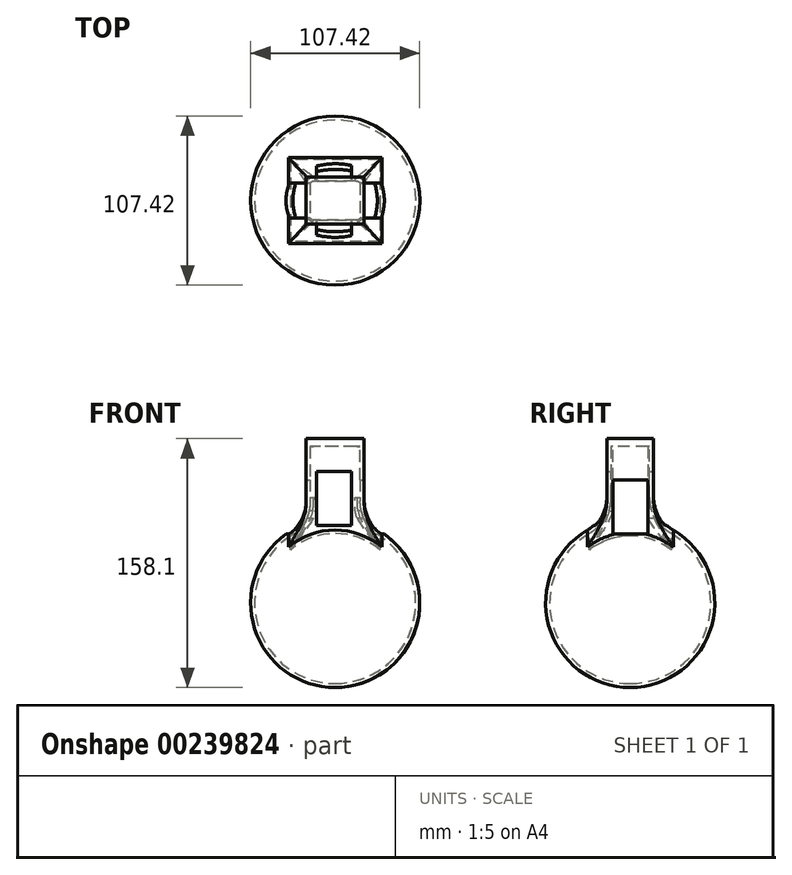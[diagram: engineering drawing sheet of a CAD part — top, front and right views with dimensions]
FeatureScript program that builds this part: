
annotation { "Feature Type Name" : "Feature", "Feature Type Description" : "" }
export const myFeature = defineFeature(function(context is Context, id is Id, definition is map)
    precondition{}
    {
        {
            var Q0;
            Q0=qCreatedBy(makeId("Front.planeOp"),FACE);
            var sketch = newSketch(context, id + "F0", { "sketchPlane" : qUnion([Q0])});
            skArc(sketch, "E0", {"start": v(0, 53.71) * mm, "mid": v(-53.71, 0) * mm, "end": v(0, -53.71) * mm});
            skLineSegment(sketch, "E1", {"start": v(0, 53.71) * mm, "end": v(0, -53.71) * mm});
            skSolve(sketch);
        }
        {
            var Q0;
            Q0 = qSketchRegion(id + "F0", true);
            var Q1;
            Q1=sQuery(id+"F0.wireOp",EDGE,"E1");
            revolve(context, id + "F1", {"entities" : qUnion([Q0]), "axis" : qUnion([Q1]), "revolveType" : RevolveType.FULL});
        }
        {
            var Q0;
            Q0=qCreatedBy(makeId("Top.planeOp"),FACE);
            var sketch = newSketch(context, id + "F2", { "sketchPlane" : qUnion([Q0])});
            skLineSegment(sketch, "E2.bottom", {"start": v(18.4, 14.82) * mm, "end": v(-18.4, 14.82) * mm});
            skLineSegment(sketch, "E2.top", {"start": v(18.4, -14.82) * mm, "end": v(-18.4, -14.82) * mm});
            skLineSegment(sketch, "E2.left", {"start": v(18.4, 14.82) * mm, "end": v(18.4, -14.82) * mm});
            skLineSegment(sketch, "E2.right", {"start": v(-18.4, 14.82) * mm, "end": v(-18.4, -14.82) * mm});
            skPoint(sketch, "E2.middle", {"position": v(0, 0) * mm});
            skSolve(sketch);
        }
        {
            var Q0;
            Q0 = qSketchRegion(id + "F2", true);
            extrude(context, id + "F3", {"entities" : qUnion([Q0]), "operationType" : NewBodyOperationType.ADD, "depth" : 99.31 * mm});
        }
        {
            var Q0;
            Q0=makeQuery(id+"F3.boolean.opBoolean","INTERSECT",EDGE,{"derivedFrom":[makeQuery(id+"F1.opRevolve","SWEPT_FACE",FACE,{"disambiguationData":[OSD([sQuery(id+"F0.wireOp",EDGE,"E0")])]}),makeQuery(id+"F3.opExtrude","SWEPT_FACE",FACE,{"disambiguationData":[OSD([sQuery(id+"F2.wireOp",EDGE,"E2.top")])]})]});
            var Q1;
            Q1=makeQuery(id+"F3.boolean.opBoolean","INTERSECT",EDGE,{"derivedFrom":[makeQuery(id+"F1.opRevolve","SWEPT_FACE",FACE,{"disambiguationData":[OSD([sQuery(id+"F0.wireOp",EDGE,"E0")])]}),makeQuery(id+"F3.opExtrude","SWEPT_FACE",FACE,{"disambiguationData":[OSD([sQuery(id+"F2.wireOp",EDGE,"E2.right")])]})]});
            var Q2;
            Q2=makeQuery(id+"F3.boolean.opBoolean","INTERSECT",EDGE,{"derivedFrom":[makeQuery(id+"F1.opRevolve","SWEPT_FACE",FACE,{"disambiguationData":[OSD([sQuery(id+"F0.wireOp",EDGE,"E0")])]}),makeQuery(id+"F3.opExtrude","SWEPT_FACE",FACE,{"disambiguationData":[OSD([sQuery(id+"F2.wireOp",EDGE,"E2.bottom")])]})]});
            var Q3;
            Q3=makeQuery(id+"F1.opRevolve","SWEPT_FACE",FACE,{"disambiguationData":[OSD([sQuery(id+"F0.wireOp",EDGE,"E0")])]});
            var Q4;
            Q4=makeQuery(id+"F3.boolean.opBoolean","INTERSECT",EDGE,{"derivedFrom":[makeQuery(id+"F1.opRevolve","SWEPT_FACE",FACE,{"disambiguationData":[OSD([sQuery(id+"F0.wireOp",EDGE,"E0")])]}),makeQuery(id+"F3.opExtrude","SWEPT_FACE",FACE,{"disambiguationData":[OSD([sQuery(id+"F2.wireOp",EDGE,"E2.left")])]})]});
            fillet(context, id + "F4", {"entities" : qUnion([Q0, Q1, Q2, Q3, Q4]), "radius" : 25.4 * mm, "tangentPropagation" : true, "allowEdgeOverflow" : false});
        }
        {
            var Q0;
            Q0=makeQuery(id+"F3.opExtrude","CAP_FACE",FACE,{"disambiguationData":[OSD([sQuery(id+"F2.wireOp",EDGE,"E2.bottom"),sQuery(id+"F2.wireOp",EDGE,"E2.top"),sQuery(id+"F2.wireOp",EDGE,"E2.left"),sQuery(id+"F2.wireOp",EDGE,"E2.right")])],"isStart":false});
            shell(context, id + "F5", {"entities" : qUnion([Q0]), "thickness" : 2.54 * mm});
        }
        {
            var Q0;
            Q0=qCreatedBy(makeId("Right.planeOp"),FACE);
            var sketch = newSketch(context, id + "F6", { "sketchPlane" : qUnion([Q0])});
            skLineSegment(sketch, "E3.bottom", {"start": v(11.14, 78.2) * mm, "end": v(-11.14, 78.2) * mm});
            skLineSegment(sketch, "E3.top", {"start": v(11.14, 43.7) * mm, "end": v(-11.14, 43.7) * mm});
            skLineSegment(sketch, "E3.left", {"start": v(11.14, 78.2) * mm, "end": v(11.14, 43.7) * mm});
            skLineSegment(sketch, "E3.right", {"start": v(-11.14, 78.2) * mm, "end": v(-11.14, 43.7) * mm});
            skPoint(sketch, "E3.middle", {"position": v(0, 60.95) * mm});
            skSolve(sketch);
        }
        {
            var Q0;
            Q0 = qSketchRegion(id + "F6", true);
            extrude(context, id + "F7", {"entities" : qUnion([Q0]), "operationType" : NewBodyOperationType.REMOVE, "endBound" : BoundingType.SYMMETRIC, "oppositeDirection" : true, "depth" : 231.65 * mm});
        }
        {
            var Q0;
            Q0=qCreatedBy(makeId("Front.planeOp"),FACE);
            var sketch = newSketch(context, id + "F8", { "sketchPlane" : qUnion([Q0])});
            skLineSegment(sketch, "E4.bottom", {"start": v(10.42, 83.58) * mm, "end": v(-11.85, 83.58) * mm});
            skLineSegment(sketch, "E4.top", {"start": v(10.42, 49.1) * mm, "end": v(-11.85, 49.1) * mm});
            skLineSegment(sketch, "E4.left", {"start": v(10.42, 83.58) * mm, "end": v(10.42, 49.1) * mm});
            skLineSegment(sketch, "E4.right", {"start": v(-11.85, 83.58) * mm, "end": v(-11.85, 49.1) * mm});
            skPoint(sketch, "E4.middle", {"position": v(-0.72, 66.34) * mm});
            skSolve(sketch);
        }
        {
            var Q0;
            Q0 = qSketchRegion(id + "F8", true);
            extrude(context, id + "F9", {"entities" : qUnion([Q0]), "operationType" : NewBodyOperationType.REMOVE, "endBound" : BoundingType.SYMMETRIC, "depth" : 368.8 * mm});
        }
        {
            var Q0;
            Q0=makeQuery(id+"F3.opExtrude","CAP_FACE",FACE,{"disambiguationData":[OSD([sQuery(id+"F2.wireOp",EDGE,"E2.bottom"),sQuery(id+"F2.wireOp",EDGE,"E2.top"),sQuery(id+"F2.wireOp",EDGE,"E2.left"),sQuery(id+"F2.wireOp",EDGE,"E2.right")])],"isStart":false});
            var sketch = newSketch(context, id + "F10", { "sketchPlane" : qUnion([Q0])});
            skSolve(sketch);
        }
        {
            var Q0;
            {var subQ3=sQuery(id+"F2.wireOp",EDGE,"E2.bottom");Q0=makeQuery(id+"F10.imprint","IMPRINT",FACE,{"disambiguationData":[TD([[makeQuery(id+"F10.imprint","IMPRINT",EDGE,{"derivedFrom":makeQuery(id+"F3.opExtrude","CAP_EDGE",EDGE,{"disambiguationData":[OSD([subQ3])],"isStart":false})}),1.0]])]});}
            var sketch = newSketch(context, id + "F11", { "sketchPlane" : qUnion([Q0])});
            skLineSegment(sketch, "E5.0", {"start": v(18.4, 14.82) * mm, "end": v(-18.4, 14.82) * mm});
            skLineSegment(sketch, "E5.1", {"start": v(-18.4, 14.82) * mm, "end": v(-18.4, -14.82) * mm});
            skLineSegment(sketch, "E5.2", {"start": v(18.4, -14.82) * mm, "end": v(-18.4, -14.82) * mm});
            skLineSegment(sketch, "E5.3", {"start": v(18.4, 14.82) * mm, "end": v(18.4, -14.82) * mm});
            skSolve(sketch);
        }
        {
            var Q0;
            Q0 = qSketchRegion(id + "F11", true);
            extrude(context, id + "F12", {"entities" : qUnion([Q0]), "operationType" : NewBodyOperationType.ADD, "depth" : 5.08 * mm});
        }
        {
            var Q0;
            {var subQ0=sQuery(id+"F2.wireOp",EDGE,"E2.left");var subQ1=sQuery(id+"F0.wireOp",EDGE,"E0");var subQ2=makeQuery(id+"F1.opRevolve","SWEPT_FACE",FACE,{"disambiguationData":[OSD([subQ1])]});var subQ3=sQuery(id+"F2.wireOp",EDGE,"E2.bottom");Q0=makeQuery(id+"F5.opShell","OFFSET_EDGE",EDGE,{"disambiguationData":[OSD([subQ1,subQ3,subQ0]),TDD([makeQuery(id+"F4.opFillet","BLEND_EDGE",EDGE,{"blendedFrom":[makeQuery(id+"F3.boolean.opBoolean","INTERSECT",EDGE,{"derivedFrom":[subQ2,makeQuery(id+"F3.opExtrude","SWEPT_FACE",FACE,{"disambiguationData":[OSD([subQ3])]})]}),makeQuery(id+"F3.boolean.opBoolean","INTERSECT",EDGE,{"derivedFrom":[subQ2,makeQuery(id+"F3.opExtrude","SWEPT_FACE",FACE,{"disambiguationData":[OSD([subQ0])]})]})],"blendedInto":[]})])]});}
            var Q1;
            {var subQ0=sQuery(id+"F2.wireOp",EDGE,"E2.right");var subQ1=sQuery(id+"F0.wireOp",EDGE,"E0");var subQ2=makeQuery(id+"F1.opRevolve","SWEPT_FACE",FACE,{"disambiguationData":[OSD([subQ1])]});var subQ3=sQuery(id+"F2.wireOp",EDGE,"E2.bottom");Q1=makeQuery(id+"F5.opShell","OFFSET_EDGE",EDGE,{"disambiguationData":[OSD([subQ1,subQ3,subQ0]),TDD([makeQuery(id+"F4.opFillet","BLEND_EDGE",EDGE,{"blendedFrom":[makeQuery(id+"F3.boolean.opBoolean","INTERSECT",EDGE,{"derivedFrom":[subQ2,makeQuery(id+"F3.opExtrude","SWEPT_FACE",FACE,{"disambiguationData":[OSD([subQ3])]})]}),makeQuery(id+"F3.boolean.opBoolean","INTERSECT",EDGE,{"derivedFrom":[subQ2,makeQuery(id+"F3.opExtrude","SWEPT_FACE",FACE,{"disambiguationData":[OSD([subQ0])]})]})],"blendedInto":[]})])]});}
            fillet(context, id + "F13", {"entities" : qUnion([Q0, Q1]), "radius" : 5.08 * mm, "tangentPropagation" : true, "allowEdgeOverflow" : false});
        }
        {
            var Q0;
            {var subQ0=sQuery(id+"F2.wireOp",EDGE,"E2.left");var subQ1=sQuery(id+"F0.wireOp",EDGE,"E0");var subQ2=makeQuery(id+"F1.opRevolve","SWEPT_FACE",FACE,{"disambiguationData":[OSD([subQ1])]});var subQ3=sQuery(id+"F2.wireOp",EDGE,"E2.top");Q0=makeQuery(id+"F5.opShell","OFFSET_EDGE",EDGE,{"disambiguationData":[OSD([subQ1,subQ3,subQ0]),TDD([makeQuery(id+"F4.opFillet","BLEND_EDGE",EDGE,{"blendedFrom":[makeQuery(id+"F3.boolean.opBoolean","INTERSECT",EDGE,{"derivedFrom":[subQ2,makeQuery(id+"F3.opExtrude","SWEPT_FACE",FACE,{"disambiguationData":[OSD([subQ3])]})]}),makeQuery(id+"F3.boolean.opBoolean","INTERSECT",EDGE,{"derivedFrom":[subQ2,makeQuery(id+"F3.opExtrude","SWEPT_FACE",FACE,{"disambiguationData":[OSD([subQ0])]})]})],"blendedInto":[]})])]});}
            var Q1;
            {var subQ0=sQuery(id+"F2.wireOp",EDGE,"E2.right");var subQ1=sQuery(id+"F0.wireOp",EDGE,"E0");var subQ2=makeQuery(id+"F1.opRevolve","SWEPT_FACE",FACE,{"disambiguationData":[OSD([subQ1])]});var subQ3=sQuery(id+"F2.wireOp",EDGE,"E2.top");Q1=makeQuery(id+"F5.opShell","OFFSET_EDGE",EDGE,{"disambiguationData":[OSD([subQ1,subQ3,subQ0]),TDD([makeQuery(id+"F4.opFillet","BLEND_EDGE",EDGE,{"blendedFrom":[makeQuery(id+"F3.boolean.opBoolean","INTERSECT",EDGE,{"derivedFrom":[subQ2,makeQuery(id+"F3.opExtrude","SWEPT_FACE",FACE,{"disambiguationData":[OSD([subQ3])]})]}),makeQuery(id+"F3.boolean.opBoolean","INTERSECT",EDGE,{"derivedFrom":[subQ2,makeQuery(id+"F3.opExtrude","SWEPT_FACE",FACE,{"disambiguationData":[OSD([subQ0])]})]})],"blendedInto":[]})])]});}
            fillet(context, id + "F14", {"entities" : qUnion([Q0, Q1]), "radius" : 2.54 * mm, "tangentPropagation" : true, "allowEdgeOverflow" : false});
        }
    });
